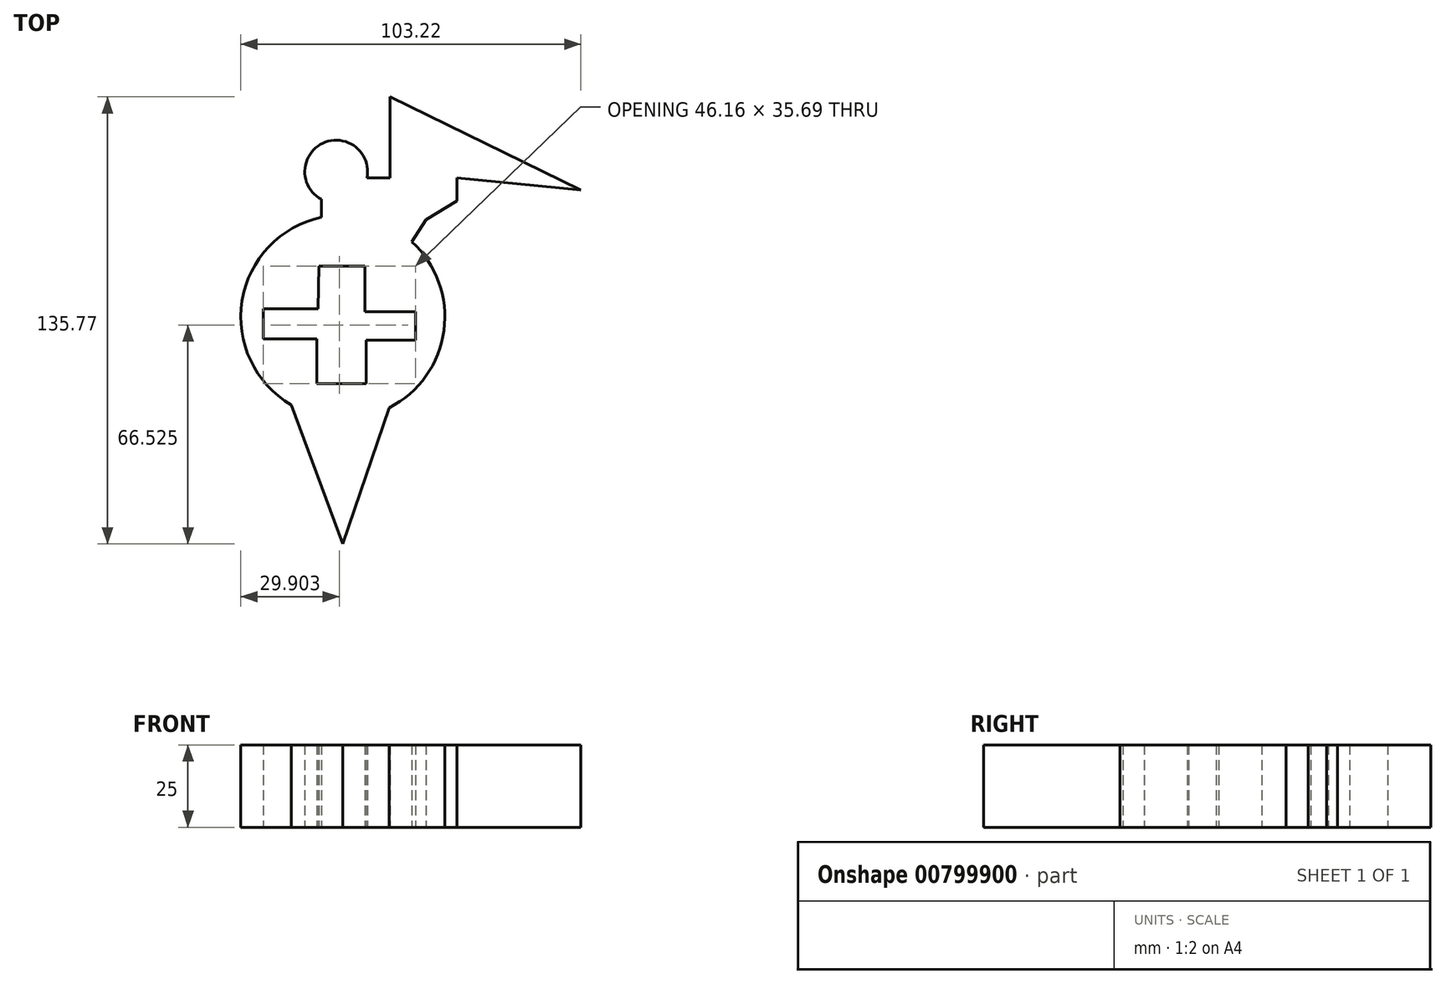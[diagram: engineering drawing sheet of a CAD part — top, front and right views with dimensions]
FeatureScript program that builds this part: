
annotation { "Feature Type Name" : "Feature", "Feature Type Description" : "" }
export const myFeature = defineFeature(function(context is Context, id is Id, definition is map)
    precondition{}
    {
        {
            var Q0;
            Q0=qCreatedBy(makeId("Top.planeOp"),FACE);
            var sketch = newSketch(context, id + "F0", { "sketchPlane" : qUnion([Q0])});
            skCircle(sketch, "E0", {"center": v(0, 0) * mm, "radius": 30.97 * mm});
            skLineSegment(sketch, "E1", {"start": v(-7.27, 15.42) * mm, "end": v(6.7, 15.42) * mm});
            skLineSegment(sketch, "E2", {"start": v(6.7, 15.42) * mm, "end": v(6.7, 1.65) * mm});
            skLineSegment(sketch, "E3", {"start": v(6.7, 1.65) * mm, "end": v(22.02, 1.65) * mm});
            skLineSegment(sketch, "E4", {"start": v(22.02, 1.65) * mm, "end": v(22.02, -7.08) * mm});
            skLineSegment(sketch, "E5", {"start": v(22.02, -7.08) * mm, "end": v(7.08, -7.08) * mm});
            skLineSegment(sketch, "E6", {"start": v(7.08, -7.08) * mm, "end": v(7.08, -20.27) * mm});
            skLineSegment(sketch, "E7", {"start": v(7.08, -20.27) * mm, "end": v(-7.86, -20.27) * mm});
            skLineSegment(sketch, "E8", {"start": v(-7.86, -20.27) * mm, "end": v(-7.86, -6.7) * mm});
            skLineSegment(sketch, "E9", {"start": v(-7.86, -6.7) * mm, "end": v(-24.15, -6.7) * mm});
            skLineSegment(sketch, "E10", {"start": v(-24.15, -6.7) * mm, "end": v(-24.15, 2.42) * mm});
            skLineSegment(sketch, "E11", {"start": v(-24.15, 2.42) * mm, "end": v(-7.47, 2.42) * mm});
            skLineSegment(sketch, "E12", {"start": v(-7.47, 2.42) * mm, "end": v(-7.27, 15.42) * mm});
            skLineSegment(sketch, "E13", {"start": v(25.31, 29.58) * mm, "end": v(34.62, 35.2) * mm});
            skLineSegment(sketch, "E14", {"start": v(34.62, 35.2) * mm, "end": v(34.62, 42.19) * mm});
            skLineSegment(sketch, "E15", {"start": v(34.62, 42.19) * mm, "end": v(72.25, 38.5) * mm});
            skLineSegment(sketch, "E16", {"start": v(72.25, 38.5) * mm, "end": v(14.26, 66.82) * mm});
            skLineSegment(sketch, "E17", {"start": v(14.26, 66.82) * mm, "end": v(14.26, 42.19) * mm});
            skCircle(sketch, "E18", {"center": v(-2.02, 44.12) * mm, "radius": 9.54 * mm});
            skLineSegment(sketch, "E19", {"start": v(-6.53, 35.71) * mm, "end": v(-6.53, 30.27) * mm});
            skLineSegment(sketch, "E20", {"start": v(5.13, 37.8) * mm, "end": v(5.13, 30.54) * mm});
            skLineSegment(sketch, "E21", {"start": v(-15.7, -26.7) * mm, "end": v(0, -68.95) * mm});
            skLineSegment(sketch, "E22", {"start": v(0, -68.95) * mm, "end": v(14.11, -27.57) * mm});
            skLineSegment(sketch, "E23", {"start": v(14.26, 42.19) * mm, "end": v(3.78, 42.19) * mm});
            skLineSegment(sketch, "E24", {"start": v(25.31, 29.58) * mm, "end": v(18.33, 18.91) * mm});
            skSolve(sketch);
        }
        {
            var Q0;
            Q0=makeQuery(id+"F0.imprint","IMPRINT",FACE,{"disambiguationData":[TD([[makeQuery(id+"F0.imprint","IMPRINT",EDGE,{"derivedFrom":sQuery(id+"F0.wireOp",EDGE,"E0")}),1.0]])]});
            var Q1;
            {var subQ0=sQuery(id+"F0.wireOp",EDGE,"E18");var subQ1=makeQuery(id+"F0.imprint","INTERSECT",VERTEX,{"derivedFrom":[subQ0,sQuery(id+"F0.wireOp",EDGE,"E19")]});Q1=makeQuery(id+"F0.imprint","IMPRINT",FACE,{"disambiguationData":[TD([[makeQuery(id+"F0.imprint","IMPRINT",EDGE,{"disambiguationData":[TD([[subQ1,-1.0]])],"derivedFrom":subQ0}),1.0]])]});}
            var Q2;
            {var subQ0=sQuery(id+"F0.wireOp",EDGE,"E19");Q2=makeQuery(id+"F0.imprint","IMPRINT",FACE,{"disambiguationData":[TD([[makeQuery(id+"F0.imprint","IMPRINT",EDGE,{"derivedFrom":subQ0}),1.0]])]});}
            var Q3;
            {var subQ0=sQuery(id+"F0.wireOp",EDGE,"E21");Q3=makeQuery(id+"F0.imprint","IMPRINT",FACE,{"disambiguationData":[TD([[makeQuery(id+"F0.imprint","IMPRINT",EDGE,{"derivedFrom":subQ0}),1.0]])]});}
            var Q4;
            {var subQ1=sQuery(id+"F0.wireOp",EDGE,"E13");Q4=makeQuery(id+"F0.imprint","IMPRINT",FACE,{"disambiguationData":[TD([[makeQuery(id+"F0.imprint","IMPRINT",EDGE,{"derivedFrom":subQ1}),1.0]])]});}
            extrude(context, id + "F1", {"entities" : qUnion([Q0, Q1, Q2, Q3, Q4]), "depth" : 25 * mm, "offsetDistance" : 25 * mm});
        }
    });
